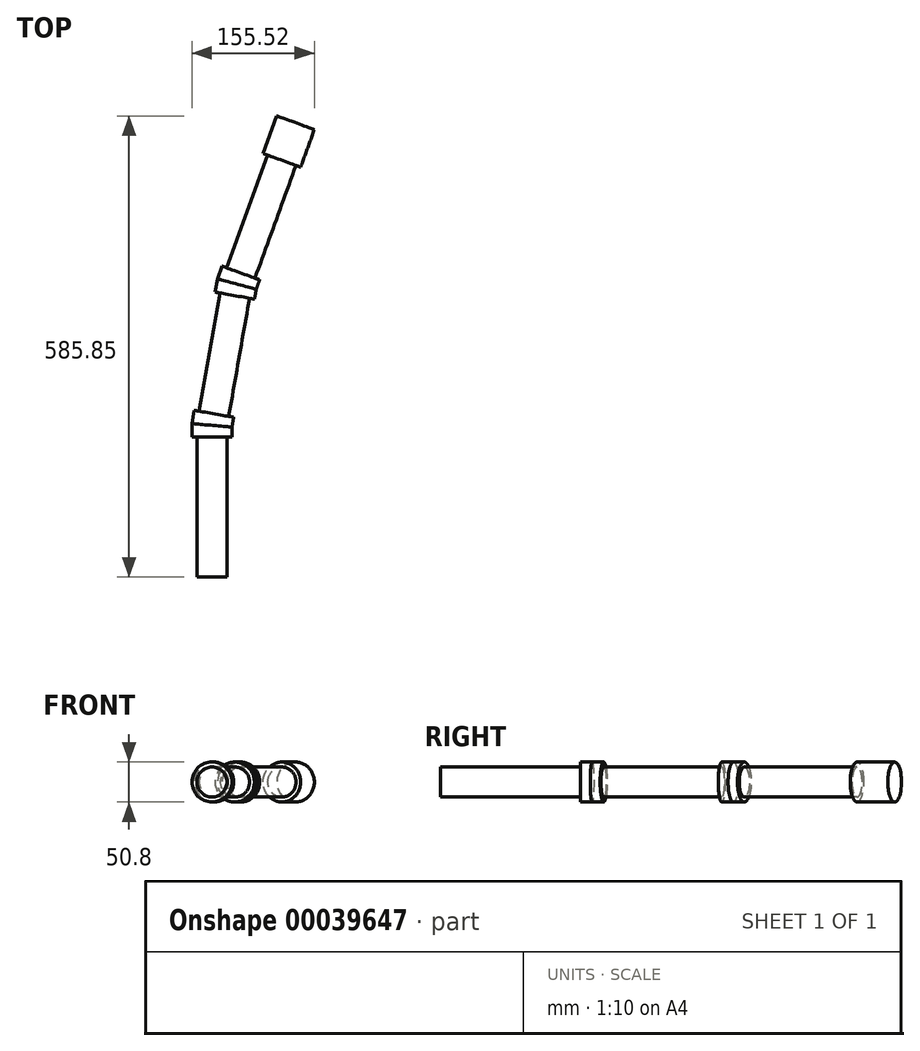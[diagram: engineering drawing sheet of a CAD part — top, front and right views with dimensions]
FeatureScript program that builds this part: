
annotation { "Feature Type Name" : "Feature", "Feature Type Description" : "" }
export const myFeature = defineFeature(function(context is Context, id is Id, definition is map)
    precondition{}
    {
        {
            var Q0;
            Q0=qCreatedBy(makeId("Top.planeOp"),FACE);
            var sketch = newSketch(context, id + "F0", { "sketchPlane" : qUnion([Q0])});
            skLineSegment(sketch, "E0", {"start": v(0, 0) * mm, "end": v(-19.05, 0) * mm});
            skLineSegment(sketch, "E1", {"start": v(0, 0) * mm, "end": v(19.05, 0) * mm});
            skLineSegment(sketch, "E2", {"start": v(19.05, 0) * mm, "end": v(19.05, 152.4) * mm});
            skLineSegment(sketch, "E3", {"start": v(-19.05, 0) * mm, "end": v(-19.05, 152.4) * mm});
            skLineSegment(sketch, "E4", {"start": v(-19.05, 152.4) * mm, "end": v(19.05, 152.4) * mm});
            skLineSegment(sketch, "E5", {"start": v(19.05, 152.4) * mm, "end": v(25.4, 152.4) * mm});
            skLineSegment(sketch, "E6", {"start": v(25.4, 152.4) * mm, "end": v(25.4, 165.1) * mm});
            skLineSegment(sketch, "E7", {"start": v(25.4, 165.1) * mm, "end": v(27.6, 177.6) * mm});
            skLineSegment(sketch, "E8", {"start": v(-19.05, 152.4) * mm, "end": v(-25.4, 152.4) * mm});
            skLineSegment(sketch, "E9", {"start": v(27.6, 177.6) * mm, "end": v(-22.42, 186.43) * mm});
            skLineSegment(sketch, "E10", {"start": v(25.4, 165.1) * mm, "end": v(-25.4, 169.54) * mm});
            skLineSegment(sketch, "E11", {"start": v(-25.4, 152.4) * mm, "end": v(-25.4, 169.54) * mm});
            skLineSegment(sketch, "E12", {"start": v(-25.4, 169.54) * mm, "end": v(-22.42, 186.43) * mm});
            skLineSegment(sketch, "E13", {"start": v(27.6, 177.6) * mm, "end": v(21.35, 178.7) * mm});
            skLineSegment(sketch, "E14", {"start": v(21.35, 178.7) * mm, "end": v(47.82, 328.8) * mm});
            skLineSegment(sketch, "E15", {"start": v(47.82, 328.8) * mm, "end": v(10.3, 335.41) * mm});
            skLineSegment(sketch, "E16", {"start": v(10.3, 335.41) * mm, "end": v(-16.17, 185.33) * mm});
            skLineSegment(sketch, "E17", {"start": v(47.82, 328.8) * mm, "end": v(54.07, 327.7) * mm});
            skLineSegment(sketch, "E18", {"start": v(54.07, 327.7) * mm, "end": v(56.27, 340.2) * mm});
            skLineSegment(sketch, "E19", {"start": v(10.3, 335.41) * mm, "end": v(4.04, 336.51) * mm});
            skLineSegment(sketch, "E20", {"start": v(56.27, 340.2) * mm, "end": v(60.62, 352.13) * mm});
            skLineSegment(sketch, "E21", {"start": v(60.62, 352.13) * mm, "end": v(12.88, 369.5) * mm});
            skLineSegment(sketch, "E22", {"start": v(56.27, 340.2) * mm, "end": v(7.02, 353.4) * mm});
            skLineSegment(sketch, "E23", {"start": v(4.04, 336.51) * mm, "end": v(7.02, 353.4) * mm});
            skLineSegment(sketch, "E24", {"start": v(7.02, 353.4) * mm, "end": v(12.88, 369.5) * mm});
            skLineSegment(sketch, "E25", {"start": v(60.62, 352.13) * mm, "end": v(54.65, 354.3) * mm});
            skLineSegment(sketch, "E26", {"start": v(54.65, 354.3) * mm, "end": v(106.78, 497.51) * mm});
            skLineSegment(sketch, "E27", {"start": v(106.78, 497.51) * mm, "end": v(112.74, 495.34) * mm});
            skLineSegment(sketch, "E28", {"start": v(130.12, 543.08) * mm, "end": v(82.38, 560.45) * mm});
            skLineSegment(sketch, "E29", {"start": v(70.97, 510.54) * mm, "end": v(18.85, 367.34) * mm});
            skLineSegment(sketch, "E30", {"start": v(70.97, 510.54) * mm, "end": v(106.78, 497.51) * mm});
            skLineSegment(sketch, "E31", {"start": v(130.12, 543.08) * mm, "end": v(112.74, 495.34) * mm});
            skLineSegment(sketch, "E32", {"start": v(82.38, 560.45) * mm, "end": v(65, 512.72) * mm});
            skLineSegment(sketch, "E33", {"start": v(65, 512.72) * mm, "end": v(70.97, 510.54) * mm});
            skSolve(sketch);
        }
        {
            var Q0;
            Q0=makeQuery(id+"F0.imprint","IMPRINT",FACE,{"disambiguationData":[TD([[makeQuery(id+"F0.imprint","IMPRINT",EDGE,{"derivedFrom":sQuery(id+"F0.wireOp",EDGE,"E20")}),1.0]])]});
            var Q1;
            Q1=makeQuery(id+"F0.imprint","IMPRINT",FACE,{"disambiguationData":[TD([[makeQuery(id+"F0.imprint","IMPRINT",EDGE,{"derivedFrom":sQuery(id+"F0.wireOp",EDGE,"E15")}),-1.0]])]});
            var Q2;
            Q2=makeQuery(id+"F0.imprint","IMPRINT",FACE,{"disambiguationData":[TD([[makeQuery(id+"F0.imprint","IMPRINT",EDGE,{"derivedFrom":sQuery(id+"F0.wireOp",EDGE,"E7")}),1.0]])]});
            var Q3;
            Q3=makeQuery(id+"F0.imprint","IMPRINT",FACE,{"disambiguationData":[TD([[makeQuery(id+"F0.imprint","IMPRINT",EDGE,{"derivedFrom":sQuery(id+"F0.wireOp",EDGE,"E4")}),1.0]])]});
            var Q4;
            Q4=makeQuery(id+"F0.imprint","IMPRINT",FACE,{"disambiguationData":[TD([[makeQuery(id+"F0.imprint","IMPRINT",EDGE,{"derivedFrom":sQuery(id+"F0.wireOp",EDGE,"E0")}),1.0]])]});
            var Q5;
            Q5=makeQuery(id+"F0.imprint","IMPRINT",FACE,{"disambiguationData":[TD([[makeQuery(id+"F0.imprint","IMPRINT",EDGE,{"derivedFrom":sQuery(id+"F0.wireOp",EDGE,"4362853a-bfab-4841-ad33-0da4945ce7d8")}),-1.0]])]});
            var Q6;
            Q6=makeQuery(id+"F0.imprint","IMPRINT",FACE,{"disambiguationData":[TD([[makeQuery(id+"F0.imprint","IMPRINT",EDGE,{"derivedFrom":sQuery(id+"F0.wireOp",EDGE,"9ec19a48-1b8f-4e76-9588-66d74d53f144")}),-1.0]])]});
            var Q7;
            Q7=makeQuery(id+"F0.imprint","IMPRINT",FACE,{"disambiguationData":[TD([[makeQuery(id+"F0.imprint","IMPRINT",EDGE,{"derivedFrom":sQuery(id+"F0.wireOp",EDGE,"E27")}),1.0]])]});
            var Q8;
            Q8=makeQuery(id+"F0.imprint","IMPRINT",FACE,{"disambiguationData":[TD([[makeQuery(id+"F0.imprint","IMPRINT",EDGE,{"derivedFrom":sQuery(id+"F0.wireOp",EDGE,"134bd195-3179-4c87-b82c-456532974db7")}),1.0]])]});
            var Q9;
            Q9=makeQuery(id+"F0.imprint","IMPRINT",FACE,{"disambiguationData":[TD([[makeQuery(id+"F0.imprint","IMPRINT",EDGE,{"derivedFrom":sQuery(id+"F0.wireOp",EDGE,"030bf412-2708-412a-a3c6-39b4ca16a0eb")}),1.0]])]});
            var Q10;
            Q10=makeQuery(id+"F0.imprint","IMPRINT",FACE,{"disambiguationData":[TD([[makeQuery(id+"F0.imprint","IMPRINT",EDGE,{"derivedFrom":sQuery(id+"F0.wireOp",EDGE,"134bd195-3179-4c87-b82c-456532974db7")}),-1.0]])]});
            var Q11;
            Q11=makeQuery(id+"F0.imprint","IMPRINT",FACE,{"disambiguationData":[TD([[makeQuery(id+"F0.imprint","IMPRINT",EDGE,{"derivedFrom":sQuery(id+"F0.wireOp",EDGE,"E28")}),-1.0]])]});
            var Q12;
            Q12=makeQuery(id+"F0.imprint","IMPRINT",FACE,{"disambiguationData":[TD([[makeQuery(id+"F0.imprint","IMPRINT",EDGE,{"derivedFrom":sQuery(id+"F0.wireOp",EDGE,"e989e8fa-5b56-48d0-8351-93b8a3e71791")}),-1.0]])]});
            extrude(context, id + "F1", {"entities" : qUnion([Q0, Q1, Q2, Q3, Q4, Q5, Q6, Q7, Q8, Q9, Q10, Q11, Q12]), "endBound" : BoundingType.SYMMETRIC, "depth" : 50.8 * mm});
        }
        {
            var Q0;
            {var subQ1=sQuery(id+"F0.wireOp",EDGE,"E26");Q0=makeQuery(id+"F0.imprint","IMPRINT",FACE,{"disambiguationData":[TD([[makeQuery(id+"F0.imprint","IMPRINT",EDGE,{"derivedFrom":subQ1}),1.0]])]});}
            var Q1;
            {var subQ1=sQuery(id+"F0.wireOp",EDGE,"E14");Q1=makeQuery(id+"F0.imprint","IMPRINT",FACE,{"disambiguationData":[TD([[makeQuery(id+"F0.imprint","IMPRINT",EDGE,{"derivedFrom":subQ1}),1.0]])]});}
            var Q2;
            Q2=makeQuery(id+"F0.imprint","IMPRINT",FACE,{"disambiguationData":[TD([[makeQuery(id+"F0.imprint","IMPRINT",EDGE,{"derivedFrom":sQuery(id+"F0.wireOp",EDGE,"E0")}),-1.0]])]});
            extrude(context, id + "F2", {"entities" : qUnion([Q0, Q1, Q2]), "endBound" : BoundingType.SYMMETRIC, "depth" : 38.1 * mm});
        }
        {
            var Q0;
            Q0=makeQuery(id+"F2.opExtrude","CAP_EDGE",EDGE,{"disambiguationData":[OSD([sQuery(id+"F0.wireOp",EDGE,"E26")])],"isStart":false});
            var Q1;
            Q1=makeQuery(id+"F2.opExtrude","CAP_EDGE",EDGE,{"disambiguationData":[OSD([sQuery(id+"F0.wireOp",EDGE,"E29")])],"isStart":false});
            var Q2;
            Q2=makeQuery(id+"F2.opExtrude","CAP_EDGE",EDGE,{"disambiguationData":[OSD([sQuery(id+"F0.wireOp",EDGE,"E14")])],"isStart":false});
            var Q3;
            Q3=makeQuery(id+"F2.opExtrude","CAP_EDGE",EDGE,{"disambiguationData":[OSD([sQuery(id+"F0.wireOp",EDGE,"E16")])],"isStart":false});
            var Q4;
            Q4=makeQuery(id+"F2.opExtrude","CAP_EDGE",EDGE,{"disambiguationData":[OSD([sQuery(id+"F0.wireOp",EDGE,"E2")])],"isStart":false});
            var Q5;
            Q5=makeQuery(id+"F2.opExtrude","CAP_EDGE",EDGE,{"disambiguationData":[OSD([sQuery(id+"F0.wireOp",EDGE,"E3")])],"isStart":false});
            var Q6;
            Q6=makeQuery(id+"F2.opExtrude","CAP_EDGE",EDGE,{"disambiguationData":[OSD([sQuery(id+"F0.wireOp",EDGE,"E2")])],"isStart":true});
            var Q7;
            Q7=makeQuery(id+"F2.opExtrude","CAP_EDGE",EDGE,{"disambiguationData":[OSD([sQuery(id+"F0.wireOp",EDGE,"E3")])],"isStart":true});
            var Q8;
            Q8=makeQuery(id+"F2.opExtrude","CAP_EDGE",EDGE,{"disambiguationData":[OSD([sQuery(id+"F0.wireOp",EDGE,"E14")])],"isStart":true});
            var Q9;
            Q9=makeQuery(id+"F2.opExtrude","CAP_EDGE",EDGE,{"disambiguationData":[OSD([sQuery(id+"F0.wireOp",EDGE,"E16")])],"isStart":true});
            var Q10;
            Q10=makeQuery(id+"F2.opExtrude","CAP_EDGE",EDGE,{"disambiguationData":[OSD([sQuery(id+"F0.wireOp",EDGE,"E26")])],"isStart":true});
            var Q11;
            Q11=makeQuery(id+"F2.opExtrude","CAP_EDGE",EDGE,{"disambiguationData":[OSD([sQuery(id+"F0.wireOp",EDGE,"E29")])],"isStart":true});
            fillet(context, id + "F3", {"entities" : qUnion([Q0, Q1, Q2, Q3, Q4, Q5, Q6, Q7, Q8, Q9, Q10, Q11]), "radius" : 19.05 * mm, "tangentPropagation" : true, "allowEdgeOverflow" : false});
        }
        {
            var Q0;
            Q0=makeQuery(id+"F1.opExtrude","CAP_EDGE",EDGE,{"disambiguationData":[OSD([sQuery(id+"F0.wireOp",EDGE,"E7")])],"isStart":false});
            var Q1;
            Q1=makeQuery(id+"F1.opExtrude","CAP_EDGE",EDGE,{"disambiguationData":[OSD([sQuery(id+"F0.wireOp",EDGE,"E12")])],"isStart":false});
            var Q2;
            Q2=makeQuery(id+"F1.opExtrude","CAP_EDGE",EDGE,{"disambiguationData":[OSD([sQuery(id+"F0.wireOp",EDGE,"E11")])],"isStart":false});
            var Q3;
            Q3=makeQuery(id+"F1.opExtrude","CAP_EDGE",EDGE,{"disambiguationData":[OSD([sQuery(id+"F0.wireOp",EDGE,"E6")])],"isStart":false});
            var Q4;
            Q4=makeQuery(id+"F1.opExtrude","CAP_EDGE",EDGE,{"disambiguationData":[OSD([sQuery(id+"F0.wireOp",EDGE,"E7")])],"isStart":true});
            var Q5;
            Q5=makeQuery(id+"F1.opExtrude","CAP_EDGE",EDGE,{"disambiguationData":[OSD([sQuery(id+"F0.wireOp",EDGE,"E6")])],"isStart":true});
            var Q6;
            Q6=makeQuery(id+"F1.opExtrude","CAP_EDGE",EDGE,{"disambiguationData":[OSD([sQuery(id+"F0.wireOp",EDGE,"E11")])],"isStart":true});
            var Q7;
            Q7=makeQuery(id+"F1.opExtrude","CAP_EDGE",EDGE,{"disambiguationData":[OSD([sQuery(id+"F0.wireOp",EDGE,"E12")])],"isStart":true});
            var Q8;
            Q8=makeQuery(id+"F1.opExtrude","CAP_EDGE",EDGE,{"disambiguationData":[OSD([sQuery(id+"F0.wireOp",EDGE,"E23")])],"isStart":true});
            var Q9;
            Q9=makeQuery(id+"F1.opExtrude","CAP_EDGE",EDGE,{"disambiguationData":[OSD([sQuery(id+"F0.wireOp",EDGE,"E24")])],"isStart":true});
            var Q10;
            Q10=makeQuery(id+"F1.opExtrude","CAP_EDGE",EDGE,{"disambiguationData":[OSD([sQuery(id+"F0.wireOp",EDGE,"E18")])],"isStart":true});
            var Q11;
            Q11=makeQuery(id+"F1.opExtrude","CAP_EDGE",EDGE,{"disambiguationData":[OSD([sQuery(id+"F0.wireOp",EDGE,"E20")])],"isStart":true});
            var Q12;
            Q12=makeQuery(id+"F1.opExtrude","CAP_EDGE",EDGE,{"disambiguationData":[OSD([sQuery(id+"F0.wireOp",EDGE,"E20")])],"isStart":false});
            var Q13;
            Q13=makeQuery(id+"F1.opExtrude","CAP_EDGE",EDGE,{"disambiguationData":[OSD([sQuery(id+"F0.wireOp",EDGE,"E24")])],"isStart":false});
            var Q14;
            Q14=makeQuery(id+"F1.opExtrude","CAP_EDGE",EDGE,{"disambiguationData":[OSD([sQuery(id+"F0.wireOp",EDGE,"E23")])],"isStart":false});
            var Q15;
            Q15=makeQuery(id+"F1.opExtrude","CAP_EDGE",EDGE,{"disambiguationData":[OSD([sQuery(id+"F0.wireOp",EDGE,"E18")])],"isStart":false});
            var Q16;
            Q16=makeQuery(id+"F1.opExtrude","CAP_EDGE",EDGE,{"disambiguationData":[OSD([sQuery(id+"F0.wireOp",EDGE,"E31")])],"isStart":false});
            var Q17;
            Q17=makeQuery(id+"F1.opExtrude","CAP_EDGE",EDGE,{"disambiguationData":[OSD([sQuery(id+"F0.wireOp",EDGE,"E31")])],"isStart":true});
            var Q18;
            Q18=makeQuery(id+"F1.opExtrude","CAP_EDGE",EDGE,{"disambiguationData":[OSD([sQuery(id+"F0.wireOp",EDGE,"E32")])],"isStart":false});
            var Q19;
            Q19=makeQuery(id+"F1.opExtrude","CAP_EDGE",EDGE,{"disambiguationData":[OSD([sQuery(id+"F0.wireOp",EDGE,"E32")])],"isStart":true});
            var Q20;
            Q20=makeQuery(id+"F1.opExtrude","CAP_EDGE",EDGE,{"disambiguationData":[OSD([sQuery(id+"F0.wireOp",EDGE,"e989e8fa-5b56-48d0-8351-93b8a3e71791")])],"isStart":false});
            var Q21;
            Q21=makeQuery(id+"F1.opExtrude","CAP_EDGE",EDGE,{"disambiguationData":[OSD([sQuery(id+"F0.wireOp",EDGE,"134bd195-3179-4c87-b82c-456532974db7")])],"isStart":false});
            var Q22;
            Q22=makeQuery(id+"F1.opExtrude","CAP_EDGE",EDGE,{"disambiguationData":[OSD([sQuery(id+"F0.wireOp",EDGE,"24408120-6648-494d-915d-874de320521e"),sQuery(id+"F0.wireOp",EDGE,"286c20bf-4efd-40d8-b315-46f60f12ca12"),sQuery(id+"F0.wireOp",EDGE,"3496fda2-568e-4d73-ae0b-d68eb73aed0e")])],"isStart":false});
            var Q23;
            Q23=makeQuery(id+"F1.opExtrude","CAP_EDGE",EDGE,{"disambiguationData":[OSD([sQuery(id+"F0.wireOp",EDGE,"134bd195-3179-4c87-b82c-456532974db7")])],"isStart":true});
            var Q24;
            Q24=makeQuery(id+"F1.opExtrude","CAP_EDGE",EDGE,{"disambiguationData":[OSD([sQuery(id+"F0.wireOp",EDGE,"e989e8fa-5b56-48d0-8351-93b8a3e71791")])],"isStart":true});
            var Q25;
            Q25=makeQuery(id+"F1.opExtrude","CAP_EDGE",EDGE,{"disambiguationData":[OSD([sQuery(id+"F0.wireOp",EDGE,"24408120-6648-494d-915d-874de320521e"),sQuery(id+"F0.wireOp",EDGE,"286c20bf-4efd-40d8-b315-46f60f12ca12"),sQuery(id+"F0.wireOp",EDGE,"3496fda2-568e-4d73-ae0b-d68eb73aed0e")])],"isStart":true});
            fillet(context, id + "F4", {"entities" : qUnion([Q0, Q1, Q2, Q3, Q4, Q5, Q6, Q7, Q8, Q9, Q10, Q11, Q12, Q13, Q14, Q15, Q16, Q17, Q18, Q19, Q20, Q21, Q22, Q23, Q24, Q25]), "radius" : 25.4 * mm, "tangentPropagation" : true, "allowEdgeOverflow" : false});
        }
        {
            var Q0;
            Q0=makeQuery(id+"F2.opExtrude","SWEPT_FACE",FACE,{"disambiguationData":[OSD([sQuery(id+"F0.wireOp",EDGE,"E0"),sQuery(id+"F0.wireOp",EDGE,"E1")])]});
            var sketch = newSketch(context, id + "F5", { "sketchPlane" : qUnion([Q0])});
            skCircle(sketch, "E34", {"center": v(0, 0) * mm, "radius": 19.05 * mm});
            skSolve(sketch);
        }
        {
            var Q0;
            Q0 = qSketchRegion(id + "F5", true);
            extrude(context, id + "F6", {"entities" : qUnion([Q0]), "operationType" : NewBodyOperationType.ADD, "depth" : 25.4 * mm});
        }
    });
